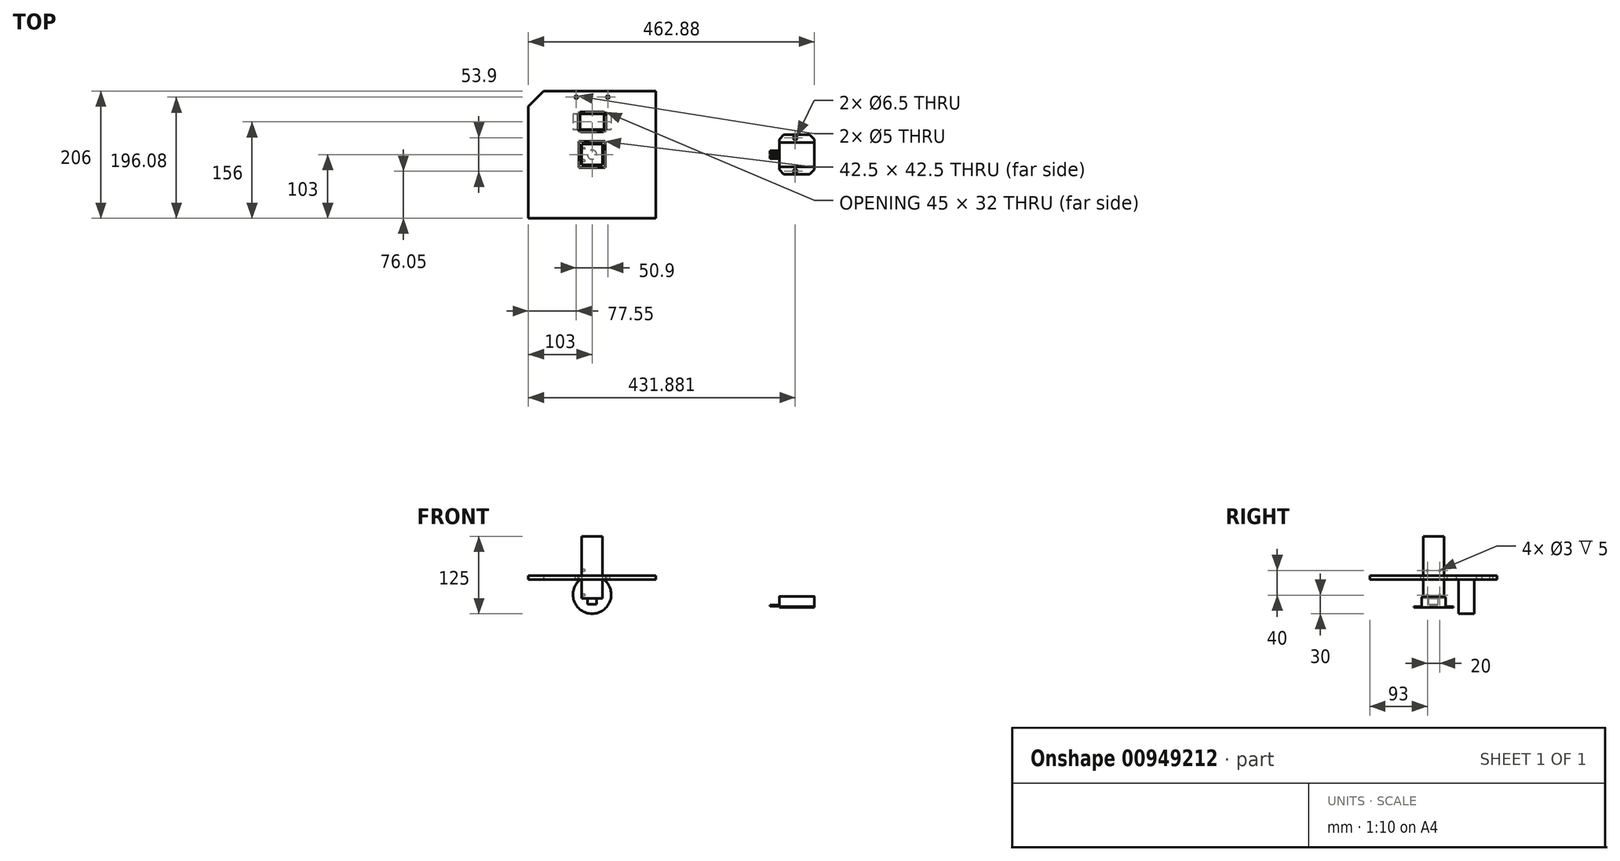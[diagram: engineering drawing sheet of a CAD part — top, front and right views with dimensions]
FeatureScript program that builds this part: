
annotation { "Feature Type Name" : "Feature", "Feature Type Description" : "" }
export const myFeature = defineFeature(function(context is Context, id is Id, definition is map)
    precondition{}
    {
        {
            var Q0;
            Q0=qCreatedBy(makeId("Front.planeOp"),FACE);
            var sketch = newSketch(context, id + "F0", { "sketchPlane" : qUnion([Q0])});
            skLineSegment(sketch, "E0", {"start": v(0, 0) * mm, "end": v(0, 15) * mm});
            skLineSegment(sketch, "E1", {"start": v(0, 15) * mm, "end": v(0, 105) * mm});
            skLineSegment(sketch, "E2", {"start": v(-20, 105) * mm, "end": v(20, 105) * mm});
            skLineSegment(sketch, "E3", {"start": v(0, 105) * mm, "end": v(0, 115) * mm});
            skLineSegment(sketch, "E4", {"start": v(-20, 115) * mm, "end": v(20, 115) * mm});
            skLineSegment(sketch, "E5", {"start": v(-20, 15) * mm, "end": v(20, 15) * mm});
            skSolve(sketch);
        }
        {
            var Q0;
            Q0=sQuery(id+"F0.wireOp",EDGE,"E5");
            cPlane(context, id + "F1", {"entities" : qUnion([Q0]), "cplaneType" : CPlaneType.LINE_ANGLE, "offset" : 25 * mm, "angle" : 90 * degree, "width" : 150 * mm, "height" : 150 * mm});
        }
        {
            var Q0;
            Q0=qCreatedBy(id+"F1.planeOp",FACE);
            var sketch = newSketch(context, id + "F2", { "sketchPlane" : qUnion([Q0])});
            skLineSegment(sketch, "E6.bottom", {"start": v(16.75, 16.75) * mm, "end": v(16.75, -16.75) * mm});
            skLineSegment(sketch, "E6.top", {"start": v(-16.75, 16.75) * mm, "end": v(-16.75, -16.75) * mm});
            skLineSegment(sketch, "E6.left", {"start": v(16.75, 16.75) * mm, "end": v(-16.75, 16.75) * mm});
            skLineSegment(sketch, "E6.right", {"start": v(16.75, -16.75) * mm, "end": v(-16.75, -16.75) * mm});
            skPoint(sketch, "E6.middle", {"position": v(0, 0) * mm});
            skSolve(sketch);
        }
        {
            var Q0;
            Q0=qCreatedBy(makeId("Top.planeOp"),FACE);
            var sketch = newSketch(context, id + "F3", { "sketchPlane" : qUnion([Q0])});
            skLineSegment(sketch, "E7", {"start": v(-53, 53) * mm, "end": v(53, 53) * mm});
            skLineSegment(sketch, "E8", {"start": v(-62.06, 78) * mm, "end": v(62.06, 78) * mm});
            skLineSegment(sketch, "E9", {"start": v(0, 0) * mm, "end": v(0, 53) * mm});
            skLineSegment(sketch, "E10", {"start": v(0, 53) * mm, "end": v(0, 78) * mm});
            skLineSegment(sketch, "E11.bottom", {"start": v(-30, 66) * mm, "end": v(30, 66) * mm});
            skLineSegment(sketch, "E11.top", {"start": v(-30, 40) * mm, "end": v(30, 40) * mm});
            skLineSegment(sketch, "E11.left", {"start": v(-30, 66) * mm, "end": v(-30, 40) * mm});
            skLineSegment(sketch, "E11.right", {"start": v(30, 66) * mm, "end": v(30, 40) * mm});
            skPoint(sketch, "E11.middle", {"position": v(0, 53) * mm});
            skLineSegment(sketch, "E12", {"start": v(0, 0) * mm, "end": v(53, 53) * mm, "construction": true});
            skLineSegment(sketch, "E13", {"start": v(0, 0) * mm, "end": v(-53, 53) * mm, "construction": true});
            skSolve(sketch);
        }
        {
            var Q0;
            Q0=sQuery(id+"F3.wireOp",EDGE,"E7");
            var Q1;
            Q1=sQuery(id+"F0.wireOp",VERTEX,"E0.start");
            cPlane(context, id + "F4", {"entities" : qUnion([Q0, Q1]), "cplaneType" : CPlaneType.LINE_ANGLE, "offset" : 25 * mm, "angle" : 90 * degree, "width" : 150 * mm, "height" : 150 * mm});
        }
        {
            var Q0;
            Q0=qCreatedBy(id+"F4.planeOp",FACE);
            var sketch = newSketch(context, id + "F5", { "sketchPlane" : qUnion([Q0])});
            skCircle(sketch, "E14", {"center": v(0, 21) * mm, "radius": 31 * mm});
            skLineSegment(sketch, "E15.bottom", {"start": v(21, 42) * mm, "end": v(-21, 42) * mm, "construction": true});
            skLineSegment(sketch, "E15.top", {"start": v(21, 0) * mm, "end": v(-21, 0) * mm, "construction": true});
            skLineSegment(sketch, "E15.left", {"start": v(21, 42) * mm, "end": v(21, 0) * mm, "construction": true});
            skLineSegment(sketch, "E15.right", {"start": v(-21, 42) * mm, "end": v(-21, 0) * mm, "construction": true});
            skSolve(sketch);
        }
        {
            var Q0;
            Q0=qCreatedBy(id+"F4.planeOp",FACE);
            var Q1;
            Q1=sQuery(id+"F3.wireOp",EDGE,"E8");
            cPlane(context, id + "F6", {"entities" : qUnion([Q0, Q1]), "cplaneType" : CPlaneType.LINE_ANGLE, "offset" : 15 * mm, "angle" : 0 * degree, "width" : 150 * mm, "height" : 150 * mm});
        }
        {
            var Q0;
            Q0=qCreatedBy(id+"F6.planeOp",FACE);
            var sketch = newSketch(context, id + "F7", { "sketchPlane" : qUnion([Q0])});
            skLineSegment(sketch, "E16.bottom", {"start": v(-21, 42) * mm, "end": v(21, 42) * mm});
            skLineSegment(sketch, "E16.top", {"start": v(-21, 0) * mm, "end": v(21, 0) * mm});
            skLineSegment(sketch, "E16.left", {"start": v(21, 42) * mm, "end": v(21, 0) * mm});
            skLineSegment(sketch, "E16.right", {"start": v(-21, 42) * mm, "end": v(-21, 0) * mm});
            skPoint(sketch, "E16.middle", {"position": v(0, 21) * mm});
            skLineSegment(sketch, "E17", {"start": v(21, 21) * mm, "end": v(-21, 21) * mm, "construction": true});
            skCircle(sketch, "E18", {"center": v(0, 21) * mm, "radius": 11.25 * mm});
            skSolve(sketch);
        }
        {
            var Q0;
            Q0=sQuery(id+"F0.wireOp",EDGE,"E4");
            var Q1;
            Q1=qCreatedBy(makeId("Top.planeOp"),FACE);
            cPlane(context, id + "F8", {"entities" : qUnion([Q0, Q1]), "cplaneType" : CPlaneType.LINE_ANGLE, "offset" : 25 * mm, "angle" : 0 * degree, "width" : 150 * mm, "height" : 150 * mm});
        }
        {
            var Q0;
            Q0=qCreatedBy(makeId("Right.planeOp"),FACE);
            var sketch = newSketch(context, id + "F9", { "sketchPlane" : qUnion([Q0])});
            skLineSegment(sketch, "E19", {"start": v(78, 21) * mm, "end": v(123, 21) * mm, "construction": true});
            skLineSegment(sketch, "E20", {"start": v(123, 42) * mm, "end": v(123, 0) * mm});
            skLineSegment(sketch, "E21", {"start": v(123, 42) * mm, "end": v(78, 42) * mm});
            skLineSegment(sketch, "E22", {"start": v(123, 0) * mm, "end": v(78, 0) * mm});
            skSolve(sketch);
        }
        {
            var Q0;
            Q0=makeQuery(id+"F2.imprint","IMPRINT",FACE,{"disambiguationData":[TD([[makeQuery(id+"F2.imprint","IMPRINT",EDGE,{"derivedFrom":sQuery(id+"F2.wireOp",EDGE,"E6.bottom")}),-1.0]])]});
            var Q1;
            Q1=qCreatedBy(id+"F8.planeOp",FACE);
            extrude(context, id + "F10", {"entities" : qUnion([Q0]), "endBound" : BoundingType.UP_TO_SURFACE, "depth" : 25 * mm, "endBoundEntityFace" : qUnion([Q1]), "offsetDistance" : 25 * mm});
        }
        {
            var Q0;
            Q0=makeQuery(id+"F5.imprint","IMPRINT",FACE,{"disambiguationData":[TD([[makeQuery(id+"F5.imprint","IMPRINT",EDGE,{"derivedFrom":sQuery(id+"F5.wireOp",EDGE,"E14")}),1.0]])]});
            extrude(context, id + "F11", {"entities" : qUnion([Q0]), "depth" : 25.5 * mm, "offsetDistance" : 25 * mm, "symmetric" : true});
        }
        {
            var Q0;
            Q0=qCreatedBy(makeId("Right.planeOp"),FACE);
            var sketch = newSketch(context, id + "F12", { "sketchPlane" : qUnion([Q0])});
            skLineSegment(sketch, "E23", {"start": v(-103, 45) * mm, "end": v(103, 45) * mm});
            skLineSegment(sketch, "E24", {"start": v(0, 45) * mm, "end": v(0, 0) * mm});
            skSolve(sketch);
        }
        {
            var Q0;
            Q0=sQuery(id+"F12.wireOp",EDGE,"E23");
            var Q1;
            Q1=qCreatedBy(makeId("Top.planeOp"),FACE);
            cPlane(context, id + "F13", {"entities" : qUnion([Q0, Q1]), "cplaneType" : CPlaneType.LINE_ANGLE, "offset" : 25 * mm, "angle" : 0 * degree, "width" : 150 * mm, "height" : 150 * mm});
        }
        {
            var Q0;
            Q0=qCreatedBy(id+"F13.planeOp",FACE);
            var sketch = newSketch(context, id + "F14", { "sketchPlane" : qUnion([Q0])});
            skLineSegment(sketch, "E25.bottom", {"start": v(-103, -103) * mm, "end": v(103, -103) * mm});
            skLineSegment(sketch, "E25.top", {"start": v(-103, 103) * mm, "end": v(103, 103) * mm});
            skLineSegment(sketch, "E25.left", {"start": v(-103, -103) * mm, "end": v(-103, 103) * mm});
            skLineSegment(sketch, "E25.right", {"start": v(103, -103) * mm, "end": v(103, 103) * mm});
            skPoint(sketch, "E25.middle", {"position": v(0, 0) * mm});
            skLineSegment(sketch, "E26.bottom", {"start": v(21.25, 21.25) * mm, "end": v(21.25, -21.25) * mm});
            skLineSegment(sketch, "E26.top", {"start": v(-21.25, 21.25) * mm, "end": v(-21.25, -21.25) * mm});
            skLineSegment(sketch, "E26.left", {"start": v(21.25, 21.25) * mm, "end": v(-21.25, 21.25) * mm});
            skLineSegment(sketch, "E26.right", {"start": v(21.25, -21.25) * mm, "end": v(-21.25, -21.25) * mm});
            skCircle(sketch, "E27", {"center": v(25.45, -93.08) * mm, "radius": 2.5 * mm, "construction": true});
            skCircle(sketch, "E28", {"center": v(-25.45, -93.08) * mm, "radius": 2.5 * mm, "construction": true});
            skLineSegment(sketch, "E29", {"start": v(-25.45, -93.08) * mm, "end": v(25.45, -93.08) * mm, "construction": true});
            skPoint(sketch, "E30", {"position": v(0, -93.08) * mm});
            skSolve(sketch);
        }
        {
            var Q0;
            Q0=makeQuery(id+"F14.imprint","IMPRINT",FACE,{"disambiguationData":[TD([[makeQuery(id+"F14.imprint","IMPRINT",EDGE,{"derivedFrom":sQuery(id+"F14.wireOp",EDGE,"E25.bottom")}),1.0]])]});
            extrude(context, id + "F15", {"entities" : qUnion([Q0]), "oppositeDirection" : true, "depth" : 6.35 * mm, "offsetDistance" : 25 * mm});
        }
        {
            var Q0;
            Q0=qCreatedBy(id+"F13.planeOp",FACE);
            var sketch = newSketch(context, id + "F16", { "sketchPlane" : qUnion([Q0])});
            skLineSegment(sketch, "E31.bottom", {"start": v(-22.5, -37) * mm, "end": v(22.5, -37) * mm});
            skLineSegment(sketch, "E31.top", {"start": v(-22.5, -69) * mm, "end": v(22.5, -69) * mm});
            skLineSegment(sketch, "E31.left", {"start": v(-22.5, -37) * mm, "end": v(-22.5, -69) * mm});
            skLineSegment(sketch, "E31.right", {"start": v(22.5, -37) * mm, "end": v(22.5, -69) * mm});
            skPoint(sketch, "E31.middle", {"position": v(0, -53) * mm});
            skSolve(sketch);
        }
        {
            var Q0;
            Q0 = qSketchRegion(id + "F16", true);
            extrude(context, id + "F17", {"entities" : qUnion([Q0]), "operationType" : NewBodyOperationType.REMOVE, "oppositeDirection" : true, "depth" : 25 * mm, "offsetDistance" : 25 * mm});
        }
        {
            var Q0;
            Q0=makeQuery(id+"F17.boolean.opBoolean","COPY",EDGE,{"derivedFrom":makeQuery(id+"F17.opExtrude","SWEPT_EDGE",EDGE,{"disambiguationData":[OSD([sQuery(id+"F16.wireOp",EDGE,"E31.bottom"),sQuery(id+"F16.wireOp",EDGE,"E31.left")])]})});
            var Q1;
            Q1=makeQuery(id+"F17.boolean.opBoolean","COPY",EDGE,{"derivedFrom":makeQuery(id+"F17.opExtrude","SWEPT_EDGE",EDGE,{"disambiguationData":[OSD([sQuery(id+"F16.wireOp",EDGE,"E31.top"),sQuery(id+"F16.wireOp",EDGE,"E31.left")])]})});
            var Q2;
            Q2=makeQuery(id+"F17.boolean.opBoolean","COPY",EDGE,{"derivedFrom":makeQuery(id+"F17.opExtrude","SWEPT_EDGE",EDGE,{"disambiguationData":[OSD([sQuery(id+"F16.wireOp",EDGE,"E31.top"),sQuery(id+"F16.wireOp",EDGE,"E31.right")])]})});
            var Q3;
            Q3=makeQuery(id+"F17.boolean.opBoolean","COPY",EDGE,{"derivedFrom":makeQuery(id+"F17.opExtrude","SWEPT_EDGE",EDGE,{"disambiguationData":[OSD([sQuery(id+"F16.wireOp",EDGE,"E31.bottom"),sQuery(id+"F16.wireOp",EDGE,"E31.right")])]})});
            fillet(context, id + "F18", {"entities" : qUnion([Q0, Q1, Q2, Q3]), "radius" : 5 * mm, "tangentPropagation" : true, "allowEdgeOverflow" : false});
        }
        {
            var Q0;
            Q0=qCreatedBy(id+"F13.planeOp",FACE);
            var sketch = newSketch(context, id + "F19", { "sketchPlane" : qUnion([Q0])});
            skCircle(sketch, "E32", {"center": v(-25.45, -93.08) * mm, "radius": 2.5 * mm});
            skCircle(sketch, "E33", {"center": v(25.45, -93.08) * mm, "radius": 2.5 * mm});
            skSolve(sketch);
        }
        {
            var Q0;
            Q0 = qSketchRegion(id + "F19", true);
            extrude(context, id + "F20", {"entities" : qUnion([Q0]), "operationType" : NewBodyOperationType.REMOVE, "oppositeDirection" : true, "depth" : 25 * mm, "offsetDistance" : 25 * mm});
        }
        {
            var Q0;
            Q0=makeQuery(id+"F10.opExtrude","SWEPT_FACE",FACE,{"disambiguationData":[OSD([sQuery(id+"F2.wireOp",EDGE,"E6.top")])]});
            var sketch = newSketch(context, id + "F21", { "sketchPlane" : qUnion([Q0])});
            skLineSegment(sketch, "E34.bottom", {"start": v(-10, 60) * mm, "end": v(10, 60) * mm, "construction": true});
            skLineSegment(sketch, "E34.top", {"start": v(-10, 20) * mm, "end": v(10, 20) * mm, "construction": true});
            skLineSegment(sketch, "E34.left", {"start": v(-10, 60) * mm, "end": v(-10, 20) * mm, "construction": true});
            skLineSegment(sketch, "E34.right", {"start": v(10, 60) * mm, "end": v(10, 20) * mm, "construction": true});
            skPoint(sketch, "E34.middle", {"position": v(0, 40) * mm});
            skCircle(sketch, "E35", {"center": v(-10, 60) * mm, "radius": 1.5 * mm});
            skCircle(sketch, "E36", {"center": v(10, 60) * mm, "radius": 1.5 * mm});
            skCircle(sketch, "E37", {"center": v(10, 20) * mm, "radius": 1.5 * mm});
            skCircle(sketch, "E38", {"center": v(-10, 20) * mm, "radius": 1.5 * mm});
            skSolve(sketch);
        }
        {
            var Q0;
            Q0=makeQuery(id+"F2.imprint","IMPRINT",FACE,{"disambiguationData":[TD([[makeQuery(id+"F2.imprint","IMPRINT",EDGE,{"derivedFrom":sQuery(id+"F2.wireOp",EDGE,"E6.bottom")}),-1.0]])]});
            var sketch = newSketch(context, id + "F22", { "sketchPlane" : qUnion([Q0])});
            skCircle(sketch, "E39", {"center": v(0, 0) * mm, "radius": 7.5 * mm});
            skSolve(sketch);
        }
        {
            var Q0;
            Q0 = qSketchRegion(id + "F22", true);
            extrude(context, id + "F23", {"entities" : qUnion([Q0]), "operationType" : NewBodyOperationType.ADD, "oppositeDirection" : true, "depth" : 10 * mm, "offsetDistance" : 25 * mm});
        }
        {
            var Q0;
            Q0 = qSketchRegion(id + "F21", true);
            extrude(context, id + "F24", {"entities" : qUnion([Q0]), "operationType" : NewBodyOperationType.REMOVE, "oppositeDirection" : true, "depth" : 10 * mm, "offsetDistance" : 25 * mm, "symmetric" : true});
        }
        {
            var Q0;
            Q0=qCreatedBy(makeId("Top.planeOp"),FACE);
            var sketch = newSketch(context, id + "F25", { "sketchPlane" : qUnion([Q0])});
            skLineSegment(sketch, "E40", {"start": v(0, 0) * mm, "end": v(-70.25, 70.25) * mm});
            skLineSegment(sketch, "E41", {"start": v(-103, 103) * mm, "end": v(-103, -103) * mm});
            skLineSegment(sketch, "E42", {"start": v(-103, -103) * mm, "end": v(103, -103) * mm});
            skLineSegment(sketch, "E43", {"start": v(103, -103) * mm, "end": v(103, 103) * mm});
            skLineSegment(sketch, "E44", {"start": v(-70.25, 70.25) * mm, "end": v(-37.5, 103) * mm});
            skLineSegment(sketch, "E45", {"start": v(-37.5, 103) * mm, "end": v(-103, 103) * mm});
            skLineSegment(sketch, "E46", {"start": v(70.25, 70.25) * mm, "end": v(37.5, 103) * mm});
            skLineSegment(sketch, "E47", {"start": v(37.5, 103) * mm, "end": v(103, 103) * mm});
            skLineSegment(sketch, "E48", {"start": v(0, 0) * mm, "end": v(70.25, 70.25) * mm});
            skSolve(sketch);
        }
        {
            var Q0;
            Q0=qCreatedBy(makeId("Top.planeOp"),FACE);
            var sketch = newSketch(context, id + "F26", { "sketchPlane" : qUnion([Q0])});
            skLineSegment(sketch, "E49.bottom", {"start": v(359.88, 32) * mm, "end": v(302.88, 32) * mm});
            skLineSegment(sketch, "E49.top", {"start": v(359.88, -32) * mm, "end": v(302.88, -32) * mm});
            skLineSegment(sketch, "E49.left", {"start": v(359.88, 32) * mm, "end": v(359.88, -32) * mm});
            skLineSegment(sketch, "E49.right", {"start": v(302.88, 32) * mm, "end": v(302.88, -32) * mm});
            skPoint(sketch, "E49.middle", {"position": v(331.38, 0) * mm});
            skSolve(sketch);
        }
        {
            var Q0;
            Q0=makeQuery(id+"F26.imprint","IMPRINT",FACE,{"disambiguationData":[TD([[makeQuery(id+"F26.imprint","IMPRINT",EDGE,{"derivedFrom":sQuery(id+"F26.wireOp",EDGE,"E49.bottom")}),1.0]])]});
            extrude(context, id + "F27", {"entities" : qUnion([Q0]), "depth" : 1.65 * mm, "offsetDistance" : 25 * mm});
        }
        {
            var Q0;
            Q0=makeQuery(id+"F27.opExtrude","SWEPT_FACE",FACE,{"disambiguationData":[OSD([sQuery(id+"F26.wireOp",EDGE,"E49.right")])]});
            var sketch = newSketch(context, id + "F28", { "sketchPlane" : qUnion([Q0])});
            skCircle(sketch, "E50", {"center": v(-5.25, 3) * mm, "radius": 1.25 * mm});
            skCircle(sketch, "E51", {"center": v(-1.75, 3) * mm, "radius": 1.25 * mm});
            skCircle(sketch, "E52", {"center": v(1.75, 3) * mm, "radius": 1.25 * mm});
            skCircle(sketch, "E53", {"center": v(5.25, 3) * mm, "radius": 1.25 * mm});
            skLineSegment(sketch, "E54", {"start": v(-5.25, 3) * mm, "end": v(-1.75, 3) * mm, "construction": true});
            skLineSegment(sketch, "E55", {"start": v(1.75, 3) * mm, "end": v(-1.75, 3) * mm, "construction": true});
            skLineSegment(sketch, "E56", {"start": v(5.25, 3) * mm, "end": v(1.75, 3) * mm, "construction": true});
            skPoint(sketch, "E57", {"position": v(0, 3) * mm});
            skSolve(sketch);
        }
        {
            var Q0;
            Q0=makeQuery(id+"F27.opExtrude","CAP_FACE",FACE,{"disambiguationData":[OSD([sQuery(id+"F26.wireOp",EDGE,"E49.bottom"),sQuery(id+"F26.wireOp",EDGE,"E49.top"),sQuery(id+"F26.wireOp",EDGE,"E49.left"),sQuery(id+"F26.wireOp",EDGE,"E49.right")])],"isStart":false});
            var sketch = newSketch(context, id + "F29", { "sketchPlane" : qUnion([Q0])});
            skLineSegment(sketch, "E58", {"start": v(302.88, 19.5) * mm, "end": v(359.88, 19.5) * mm});
            skLineSegment(sketch, "E59", {"start": v(359.88, 19.5) * mm, "end": v(359.88, -19.5) * mm});
            skLineSegment(sketch, "E60", {"start": v(359.88, -19.5) * mm, "end": v(302.88, -19.5) * mm});
            skLineSegment(sketch, "E61", {"start": v(302.88, -19.5) * mm, "end": v(302.88, 19.5) * mm});
            skPoint(sketch, "E62", {"position": v(359.88, 0) * mm});
            skSolve(sketch);
        }
        {
            var Q0;
            Q0 = qSketchRegion(id + "F29", true);
            extrude(context, id + "F30", {"entities" : qUnion([Q0]), "operationType" : NewBodyOperationType.ADD, "depth" : 16 * mm, "offsetDistance" : 25 * mm});
        }
        {
            var Q0;
            Q0=makeQuery(id+"F30.opExtrude","CAP_EDGE",EDGE,{"disambiguationData":[OSD([sQuery(id+"F29.wireOp",EDGE,"E58")])],"isStart":false});
            var Q1;
            Q1=makeQuery(id+"F30.opExtrude","CAP_EDGE",EDGE,{"disambiguationData":[OSD([sQuery(id+"F29.wireOp",EDGE,"E60")])],"isStart":false});
            fillet(context, id + "F31", {"entities" : qUnion([Q0, Q1]), "tangentPropagation" : true, "radius" : 2.5 * mm, "defaultsChanged" : true, "vertexSettings" : [], "allowEdgeOverflow" : false});
        }
        {
            var Q0;
            Q0 = qSketchRegion(id + "F28", true);
            extrude(context, id + "F32", {"entities" : qUnion([Q0]), "operationType" : NewBodyOperationType.ADD, "depth" : 15 * mm, "offsetDistance" : 25 * mm});
        }
        {
            var Q0;
            Q0=makeQuery(id+"F27.opExtrude","SWEPT_EDGE",EDGE,{"disambiguationData":[OSD([sQuery(id+"F26.wireOp",EDGE,"E49.bottom"),sQuery(id+"F26.wireOp",EDGE,"E49.right")])]});
            var Q1;
            Q1=makeQuery(id+"F27.opExtrude","SWEPT_EDGE",EDGE,{"disambiguationData":[OSD([sQuery(id+"F26.wireOp",EDGE,"E49.top"),sQuery(id+"F26.wireOp",EDGE,"E49.right")])]});
            var Q2;
            Q2=makeQuery(id+"F27.opExtrude","SWEPT_EDGE",EDGE,{"disambiguationData":[OSD([sQuery(id+"F26.wireOp",EDGE,"E49.bottom"),sQuery(id+"F26.wireOp",EDGE,"E49.left")])]});
            var Q3;
            Q3=makeQuery(id+"F27.opExtrude","SWEPT_EDGE",EDGE,{"disambiguationData":[OSD([sQuery(id+"F26.wireOp",EDGE,"E49.top"),sQuery(id+"F26.wireOp",EDGE,"E49.left")])]});
            chamfer(context, id + "F33", {"entities" : qUnion([Q0, Q1, Q2, Q3]), "width" : 7.5 * mm});
        }
        {
            var Q0;
            Q0=makeQuery(id+"F27.opExtrude","CAP_FACE",FACE,{"disambiguationData":[OSD([sQuery(id+"F26.wireOp",EDGE,"E49.bottom"),sQuery(id+"F26.wireOp",EDGE,"E49.top"),sQuery(id+"F26.wireOp",EDGE,"E49.left"),sQuery(id+"F26.wireOp",EDGE,"E49.right")])],"isStart":true});
            var sketch = newSketch(context, id + "F34", { "sketchPlane" : qUnion([Q0])});
            skCircle(sketch, "E63", {"center": v(328.88, 26.95) * mm, "radius": 3.25 * mm});
            skCircle(sketch, "E64", {"center": v(328.88, -26.95) * mm, "radius": 3.25 * mm});
            skLineSegment(sketch, "E65", {"start": v(328.88, 26.95) * mm, "end": v(328.88, -26.95) * mm, "construction": true});
            skLineSegment(sketch, "E66", {"start": v(302.88, 0) * mm, "end": v(328.88, 0) * mm, "construction": true});
            skSolve(sketch);
        }
        {
            var Q0;
            Q0 = qSketchRegion(id + "F34", true);
            extrude(context, id + "F35", {"entities" : qUnion([Q0]), "operationType" : NewBodyOperationType.REMOVE, "oppositeDirection" : true, "depth" : 25 * mm, "offsetDistance" : 25 * mm});
        }
        {
            var Q0;
            Q0=qCreatedBy(id+"F13.planeOp",FACE);
            var sketch = newSketch(context, id + "F36", { "sketchPlane" : qUnion([Q0])});
            skLineSegment(sketch, "E67", {"start": v(-78.25, -103) * mm, "end": v(-103, -78.25) * mm});
            skLineSegment(sketch, "E68", {"start": v(-103, -78.25) * mm, "end": v(-78.25, -103) * mm});
            skLineSegment(sketch, "E69", {"start": v(-78.25, -103) * mm, "end": v(-78.25, -103) * mm});
            skLineSegment(sketch, "E70", {"start": v(-103, -103) * mm, "end": v(-103, -78.25) * mm});
            skLineSegment(sketch, "E71", {"start": v(-103, -103) * mm, "end": v(-78.25, -103) * mm});
            skSolve(sketch);
        }
        {
            var Q0;
            Q0 = qSketchRegion(id + "F36", true);
            extrude(context, id + "F37", {"entities" : qUnion([Q0]), "operationType" : NewBodyOperationType.REMOVE, "oppositeDirection" : true, "depth" : 25 * mm, "offsetDistance" : 25 * mm});
        }
        {
            var Q0;
            Q0=sQuery(id+"F3.wireOp",EDGE,"E12");
            var Q1;
            Q1=qCreatedBy(makeId("Top.planeOp"),FACE);
            cPlane(context, id + "F38", {"entities" : qUnion([Q0, Q1]), "cplaneType" : CPlaneType.LINE_ANGLE, "offset" : 25 * mm, "angle" : 90 * degree, "width" : 150 * mm, "height" : 150 * mm});
        }
        {
            var Q0;
            Q0=qCreatedBy(id+"F38.planeOp",FACE);
            var sketch = newSketch(context, id + "F39", { "sketchPlane" : qUnion([Q0])});
            skLineSegment(sketch, "E72", {"start": v(-128, 80) * mm, "end": v(-128, 5) * mm});
            skLineSegment(sketch, "E73", {"start": v(-22, 120) * mm, "end": v(-22, 0) * mm, "construction": true});
            skLineSegment(sketch, "E74", {"start": v(-22, 120) * mm, "end": v(0, 120) * mm});
            skLineSegment(sketch, "E75", {"start": v(0, 120) * mm, "end": v(0, 0) * mm, "construction": true});
            skLineSegment(sketch, "E76", {"start": v(-22, 120) * mm, "end": v(-128, 80) * mm});
            skLineSegment(sketch, "E77", {"start": v(-128, 5) * mm, "end": v(0, 5) * mm});
            skLineSegment(sketch, "E78", {"start": v(0, 5) * mm, "end": v(0, 120) * mm});
            skLineSegment(sketch, "E79", {"start": v(-128, 80) * mm, "end": v(0, 80) * mm, "construction": true});
            skSolve(sketch);
        }
        {
            var Q0;
            Q0=qCreatedBy(makeId("Right.planeOp"),FACE);
            var sketch = newSketch(context, id + "F40", { "sketchPlane" : qUnion([Q0])});
            skLineSegment(sketch, "E80", {"start": v(0, 120) * mm, "end": v(18.75, 120) * mm});
            skLineSegment(sketch, "E81", {"start": v(18.75, 120) * mm, "end": v(103, 80) * mm});
            skLineSegment(sketch, "E82", {"start": v(103, 80) * mm, "end": v(103, 5) * mm});
            skLineSegment(sketch, "E83", {"start": v(103, 5) * mm, "end": v(0, 5) * mm});
            skLineSegment(sketch, "E84", {"start": v(0, 5) * mm, "end": v(0, 120) * mm});
            skSolve(sketch);
        }
        {
            var Q0;
            Q0=sQuery(id+"F39.wireOp",EDGE,"E74");
            var Q1;
            Q1=qCreatedBy(makeId("Right.planeOp"),FACE);
            cPlane(context, id + "F41", {"entities" : qUnion([Q0, Q1]), "cplaneType" : CPlaneType.LINE_ANGLE, "offset" : 25 * mm, "angle" : 90 * degree, "width" : 150 * mm, "height" : 150 * mm});
        }
        {
            var Q0;
            Q0=sQuery(id+"F39.wireOp",VERTEX,"E79.end");
            var Q1;
            Q1=sQuery(id+"F39.wireOp",VERTEX,"E72.start");
            var Q2;
            Q2=sQuery(id+"F40.wireOp",VERTEX,"E81.end");
            cPlane(context, id + "F42", {"entities" : qUnion([Q0, Q1, Q2]), "cplaneType" : CPlaneType.THREE_POINT, "offset" : 25 * mm, "width" : 150 * mm, "height" : 150 * mm});
        }
    });
